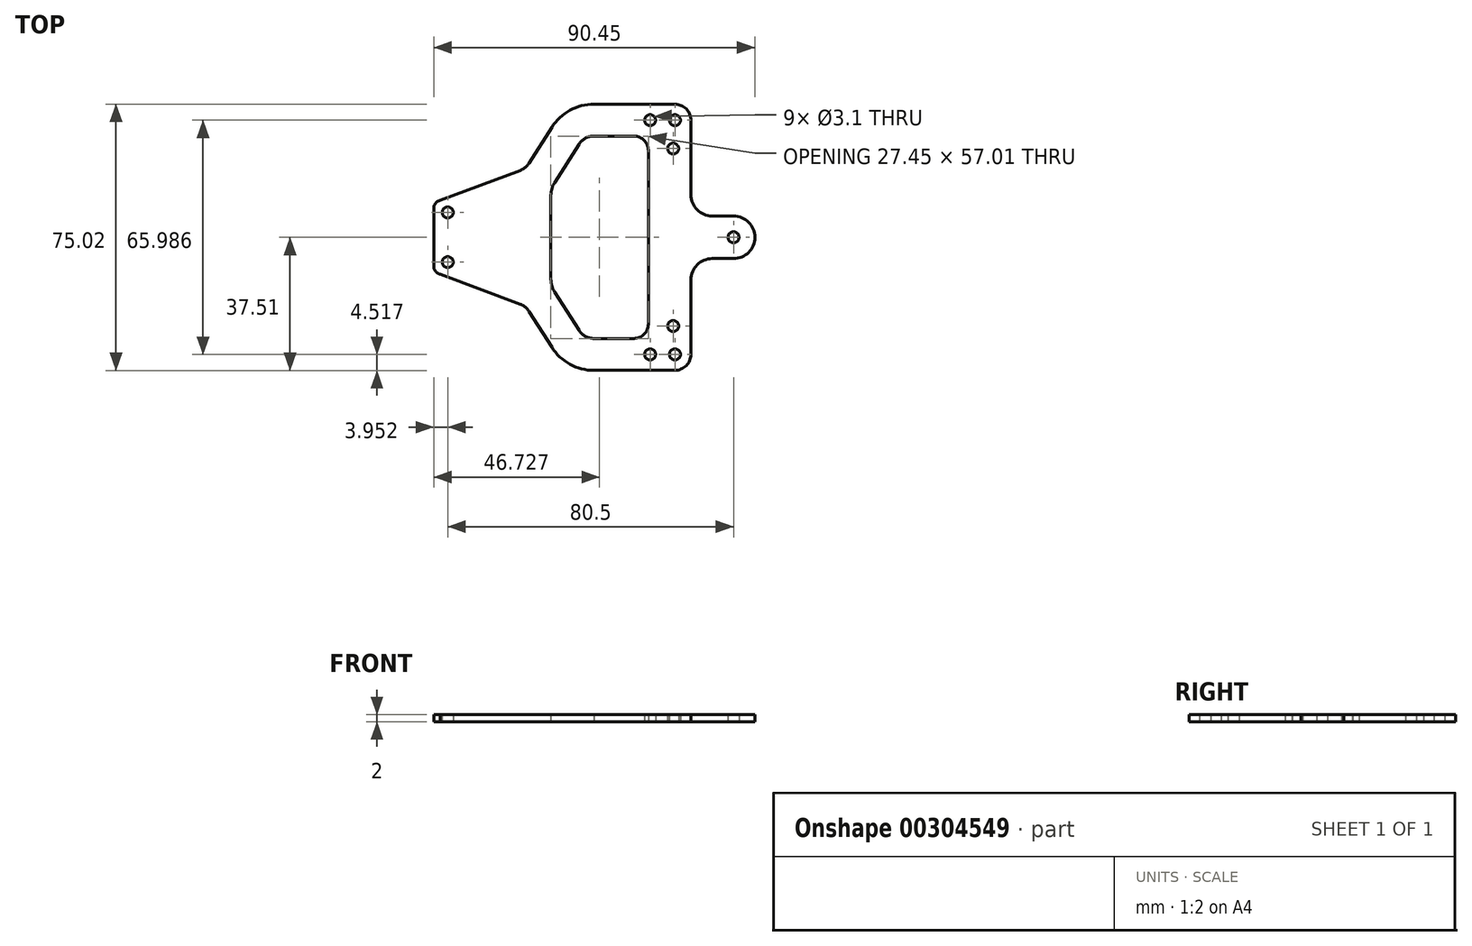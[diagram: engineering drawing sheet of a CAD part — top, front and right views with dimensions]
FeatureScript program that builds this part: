
annotation { "Feature Type Name" : "Feature", "Feature Type Description" : "" }
export const myFeature = defineFeature(function(context is Context, id is Id, definition is map)
    precondition{}
    {
        {
            var Q0;
            Q0=qCreatedBy(makeId("Top.planeOp"),FACE);
            var sketch = newSketch(context, id + "F0", { "sketchPlane" : qUnion([Q0])});
            skLineSegment(sketch, "E0.bottom", {"start": v(0, 0) * mm, "end": v(0, 0) * mm});
            skLineSegment(sketch, "E0.top", {"start": v(0, 0) * mm, "end": v(0, 0) * mm});
            skLineSegment(sketch, "E0.left", {"start": v(0, 0) * mm, "end": v(0, 0) * mm});
            skLineSegment(sketch, "E0.right", {"start": v(0, 0) * mm, "end": v(0, 0) * mm});
            skPoint(sketch, "E1.middle", {"position": v(0, 0) * mm});
            skArc(sketch, "E2.filletArc", {"start": v(24.13, 33) * mm, "mid": v(22.8, 36.17) * mm, "end": v(19.64, 37.49) * mm});
            skCircle(sketch, "E3", {"center": v(19.63, 32.99) * mm, "radius": 1.55 * mm});
            skCircle(sketch, "E4", {"center": v(12.63, 33) * mm, "radius": 1.55 * mm});
            skCircle(sketch, "E5", {"center": v(-44.37, 7) * mm, "radius": 1.55 * mm});
            skArc(sketch, "E6.filletArc", {"start": v(-46.53, 10.41) * mm, "mid": v(-47.7, 9.7) * mm, "end": v(-48.32, 8.48) * mm});
            skLineSegment(sketch, "E7", {"start": v(-48.32, 8.48) * mm, "end": v(-48.32, -8.48) * mm});
            skLineSegment(sketch, "E8", {"start": v(-46.53, 10.41) * mm, "end": v(-23.93, 18.85) * mm});
            skArc(sketch, "E9.filletArc", {"start": v(-23.93, 18.85) * mm, "mid": v(-22.52, 19.66) * mm, "end": v(-21.44, 20.88) * mm});
            skLineSegment(sketch, "E10", {"start": v(-7.43, 26.18) * mm, "end": v(-14.23, 15.43) * mm});
            skArc(sketch, "E11.filletArc", {"start": v(-3.14, 28.5) * mm, "mid": v(-5.59, 27.9) * mm, "end": v(-7.43, 26.18) * mm});
            skLineSegment(sketch, "E12", {"start": v(-15.32, 11.69) * mm, "end": v(-15.32, -11.77) * mm});
            skArc(sketch, "E13.filletArc", {"start": v(-14.23, 15.43) * mm, "mid": v(-15.04, 13.64) * mm, "end": v(-15.32, 11.69) * mm});
            skLineSegment(sketch, "E14", {"start": v(24.13, 33) * mm, "end": v(24.13, 12) * mm});
            skPoint(sketch, "E15.visualSharp", {"position": v(-11, 37.5) * mm});
            skArc(sketch, "E16.filletArc", {"start": v(-3.16, 37.5) * mm, "mid": v(-9.95, 35.77) * mm, "end": v(-15.05, 30.97) * mm});
            skLineSegment(sketch, "E17", {"start": v(-21.44, 20.88) * mm, "end": v(-15.05, 30.97) * mm});
            skLineSegment(sketch, "E18", {"start": v(-3.16, 37.5) * mm, "end": v(19.64, 37.49) * mm});
            skLineSegment(sketch, "E19.MirrorCS", {"start": v(-3.16, -37.5) * mm, "end": v(19.64, -37.49) * mm});
            skCircle(sketch, "E20.MirrorC", {"center": v(19.63, -32.99) * mm, "radius": 1.55 * mm});
            skLineSegment(sketch, "E21.MirrorCS", {"start": v(24.13, -32.99) * mm, "end": v(24.13, -12) * mm});
            skArc(sketch, "E22.MirrorCS", {"start": v(-3.16, -37.5) * mm, "mid": v(-9.95, -35.77) * mm, "end": v(-15.05, -30.97) * mm});
            skLineSegment(sketch, "E23.MirrorCS", {"start": v(-21.44, -20.88) * mm, "end": v(-15.05, -30.97) * mm});
            skArc(sketch, "E24.MirrorCS", {"start": v(-23.93, -18.85) * mm, "mid": v(-22.52, -19.66) * mm, "end": v(-21.44, -20.88) * mm});
            skLineSegment(sketch, "E25.MirrorCS", {"start": v(-46.53, -10.41) * mm, "end": v(-23.93, -18.85) * mm});
            skArc(sketch, "E26.MirrorCS", {"start": v(-46.53, -10.41) * mm, "mid": v(-47.7, -9.7) * mm, "end": v(-48.32, -8.48) * mm});
            skArc(sketch, "E27.MirrorCS", {"start": v(-14.23, -15.43) * mm, "mid": v(-15.04, -13.64) * mm, "end": v(-15.32, -11.69) * mm});
            skLineSegment(sketch, "E28.MirrorCS", {"start": v(-7.43, -26.18) * mm, "end": v(-14.23, -15.43) * mm});
            skArc(sketch, "E29.MirrorCS", {"start": v(-3.14, -28.5) * mm, "mid": v(-5.59, -27.9) * mm, "end": v(-7.43, -26.18) * mm});
            skCircle(sketch, "E30.MirrorC", {"center": v(12.63, -33) * mm, "radius": 1.55 * mm});
            skCircle(sketch, "E31.MirrorC", {"center": v(-44.37, -7) * mm, "radius": 1.55 * mm});
            skCircle(sketch, "E32", {"center": v(19.13, -25) * mm, "radius": 1.55 * mm});
            skCircle(sketch, "E33.MirrorC", {"center": v(19.13, 25) * mm, "radius": 1.55 * mm});
            skCircle(sketch, "E34", {"center": v(36.13, 0) * mm, "radius": 1.55 * mm});
            skLineSegment(sketch, "E35", {"start": v(42.13, 0) * mm, "end": v(42.13, 0) * mm});
            skLineSegment(sketch, "E36", {"start": v(-3.14, 28.5) * mm, "end": v(8.14, 28.5) * mm});
            skPoint(sketch, "E37.visualSharp", {"position": v(13.13, 28.5) * mm});
            skArc(sketch, "E37.filletArc", {"start": v(12.13, 24.5) * mm, "mid": v(10.96, 27.32) * mm, "end": v(8.14, 28.5) * mm});
            skLineSegment(sketch, "E38", {"start": v(-3.14, -28.5) * mm, "end": v(8.13, -28.5) * mm});
            skLineSegment(sketch, "E39", {"start": v(12.13, 24.5) * mm, "end": v(12.13, -24.5) * mm});
            skPoint(sketch, "E40.visualSharp", {"position": v(12.13, -28.5) * mm});
            skArc(sketch, "E40.filletArc", {"start": v(8.13, -28.5) * mm, "mid": v(10.96, -27.33) * mm, "end": v(12.13, -24.5) * mm});
            skLineSegment(sketch, "E41", {"start": v(24.13, -12) * mm, "end": v(24.13, -12) * mm});
            skLineSegment(sketch, "E42", {"start": v(30.13, -6) * mm, "end": v(36.13, -6) * mm});
            skLineSegment(sketch, "E43", {"start": v(24.13, 12) * mm, "end": v(24.13, 12) * mm});
            skLineSegment(sketch, "E44", {"start": v(30.13, 6) * mm, "end": v(36.13, 6) * mm});
            skPoint(sketch, "E45.visualSharp", {"position": v(42.13, -6) * mm});
            skArc(sketch, "E45.filletArc", {"start": v(36.13, -6) * mm, "mid": v(40.37, -4.24) * mm, "end": v(42.13, 0) * mm});
            skPoint(sketch, "E46.visualSharp", {"position": v(42.13, 6) * mm});
            skArc(sketch, "E46.filletArc", {"start": v(42.13, 0) * mm, "mid": v(40.37, 4.24) * mm, "end": v(36.13, 6) * mm});
            skPoint(sketch, "E47.visualSharp", {"position": v(24.13, -6) * mm});
            skArc(sketch, "E47.filletArc", {"start": v(30.13, -6) * mm, "mid": v(25.89, -7.76) * mm, "end": v(24.13, -12) * mm});
            skPoint(sketch, "E48.visualSharp", {"position": v(24.13, 6) * mm});
            skArc(sketch, "E48.filletArc", {"start": v(24.13, 12) * mm, "mid": v(25.89, 7.76) * mm, "end": v(30.13, 6) * mm});
            skArc(sketch, "E49.filletArc", {"start": v(19.64, -37.49) * mm, "mid": v(22.82, -36.17) * mm, "end": v(24.13, -32.99) * mm});
            skSolve(sketch);
        }
        {
            var Q0;
            Q0=qSketchRegion(id+"F0",true);
            extrude(context, id + "F1", {"entities" : qUnion([Q0]), "depth" : 2 * mm});
        }
    });
